# Revit family: DC_Rheem_PLM_CPE3_FreeStanding
name_source: partatom
category: Plumbing Fixtures
revit_build: Autodesk Revit 2018 (Build: 20170223_1515(x64)
units: mm (PartAtom-declared; Revit-internal decimal feet)

## family parameters
Cut with Voids When Loaded = No
Host = Face
Part Type = Normal
Room Calculation Point = No
Round Connector Dimension = Use Radius
Shared = No

## types (2) — shared parameters
Cold Water Pipe Diameter = 40 mm  [stored 0.131234 ft]
ColdWaterPipeRadius_ANZRS = 20 mm  [stored 0.0656168 ft]
Description = Commpak - Gas Continuous Flow- Outdoor - 615 MJ/h Propane gas free standing frame - single pump - recirculation and dead leg 60°C +
GasPipeDiameterD3_ANZRS = 40 mm  [stored 0.131234 ft]
GasPipeRadius_ANZRS = 20 mm  [stored 0.0656168 ft]
HotWaterOutletDiameterD2_ANZRS = 40 mm  [stored 0.131234 ft]
HotWaterOutletRadius_ANZRS = 20 mm  [stored 0.0656168 ft]
HotWaterReturnDiameterD1_ANZRS = 25 mm  [stored 0.082021 ft]
HotWaterReturnRadius_ANZRS = 12.5 mm  [stored 0.0410105 ft]
Length_ANZRS = 1076 mm
Manufacturer = Rheem
Material_ANZRS = Rheem - Antique White
Materials_ANZRS = Rheem - Antique White
Type Comments = 41L/min @ 50°C rise  - Separate secondary recirculation pump not required. Optional dual pump and controller available, quote part no. 299659.
URL = http://www.rheem.com.au
zero-valued in all types: Default Elevation

## per-type parameters (varying)
| type | HotWaterRadius_ANZRS |
| CPE03NK | 0 mm  [stored 0 ft] |
| CPE03PK | 20 mm  [stored 0.0656168 ft] |

note: column(s) folded — value = type name in every type: Model

note: [stored X ft] marks values corroborated as IEEE doubles in the binary element streams (Revit-internal decimal feet)

## geometry (parser evidence)
native form markers: Blend x6, Sweep x18
no freeform markers — native parametric forms only
